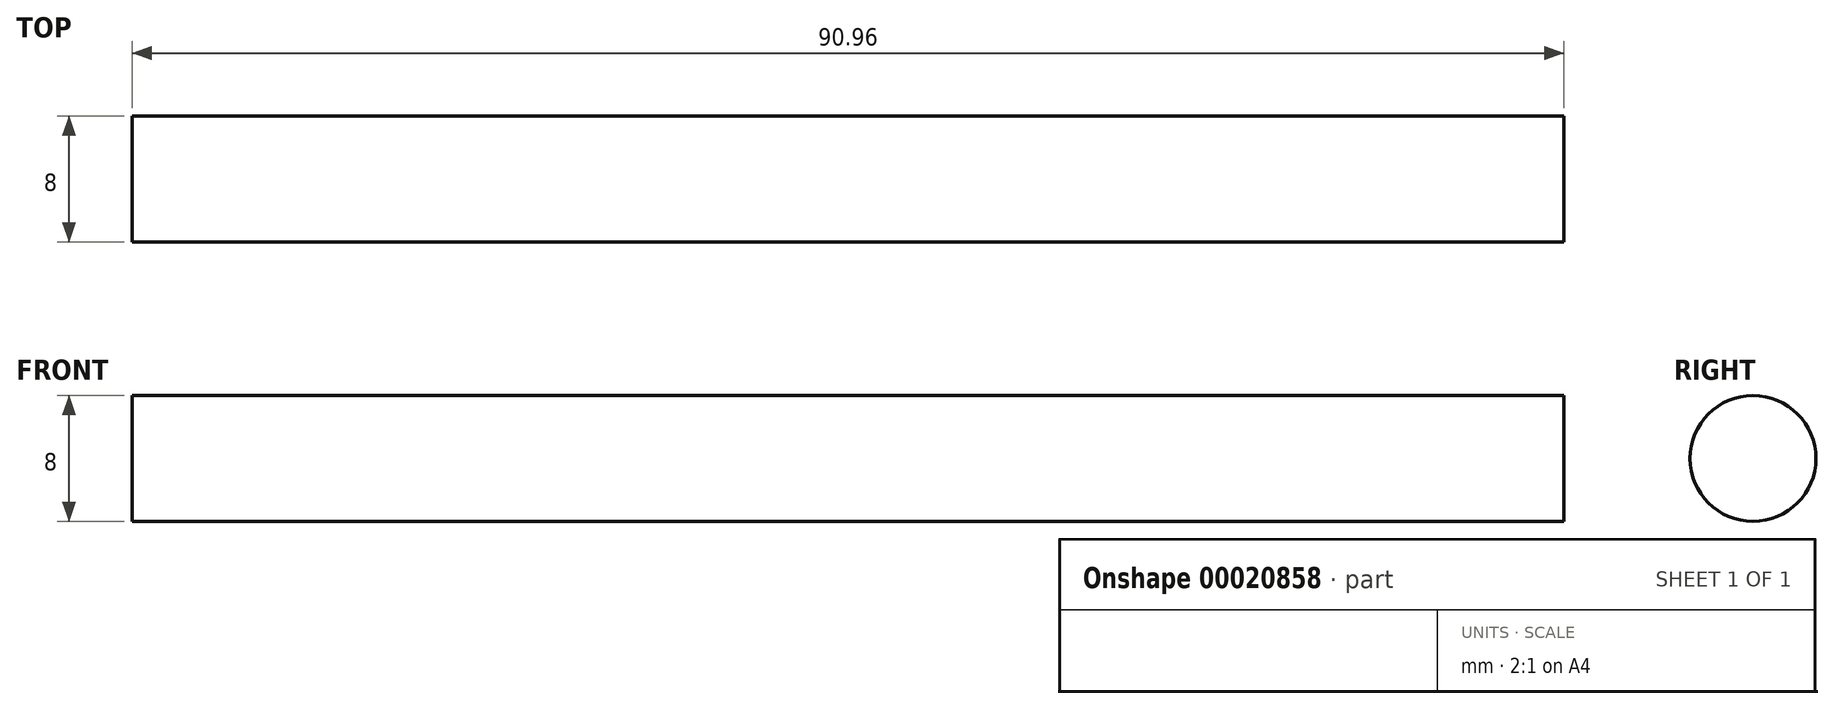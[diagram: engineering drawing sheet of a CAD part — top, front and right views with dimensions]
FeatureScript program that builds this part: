
annotation { "Feature Type Name" : "Feature", "Feature Type Description" : "" }
export const myFeature = defineFeature(function(context is Context, id is Id, definition is map)
    precondition{}
    {
        {
            var Q0;
            Q0=qCreatedBy(makeId("Right.planeOp"),FACE);
            var sketch = newSketch(context, id + "F0", { "sketchPlane" : qUnion([Q0])});
            skCircle(sketch, "E0", {"center": v(0, 0) * mm, "radius": 4 * mm});
            skSolve(sketch);
        }
        {
            var Q0;
            Q0 = qSketchRegion(id + "F0", true);
            extrude(context, id + "F1", {"entities" : qUnion([Q0]), "endBound" : BoundingType.SYMMETRIC, "depth" : 90.96 * mm});
        }
    });
